# Revit family: IS_Strada_K0776_BIM_BE
name_source: partatom
category: Plumbing Fixtures
revit_build: Autodesk Revit 2015 (Build: 20140606_1530(x64)
units: mm (PartAtom-declared; Revit-internal decimal feet)

## types (1)
- K077601 - Strada Lavabo à poser 50 cm sans vidage
    Accesoires = www.idealstandard.be
    Afwerking = Wit
    Auteur = Ideal Standard Produktions-GmbH
    Barcode = 4015413031363
    Beschrijvinggarantie = Fabrieksgarantie
    BimObjectNaam = ISI_IdealStandard_Lavabo_Strada_K077601
    Breedte = 0
    BrutoGewicht = 0
    Cost = 0 $
    Default Elevation = 0 mm  [stored 0 ft]
    Description = Strada Lavabo à poser 50 cm sans vidage
    Diepte = 0 mm  [stored 0 ft]
    Dimensions = 420 x 500 x 115 mm
    DuurEenheid = jaar
    Eigenschappen = Strada opbouwwastafel 500 mm uit fijne vuurklei. Achterzijde is geglazuurd. Zonder kraangaten of overloop. Te combineren met verhoogde wastafelkraan of muurkraan en een niet afsluitbare waste.
    Garantieonderdelen = 10
    GrootteAfvoergat = 0
    Hauteur = 115 mm
    IfcExportAs = IfcSanitaryTerminalType
    IfcExportType = WASHHANDBASINS
    Installatieinstructies = www.idealstandard.be
    Kleur = Wit
    Largeur = 500 mm
    Lengte = 0 mm  [stored 0 ft]
    Longueur = 420 mm
    Manufacturer = www.idealstandard.be
    Materiaal = fijne vuurklei
    MaterialFinish = IS_IdealStandard_Ceramic_White_Render
    Merk = Ideal Standard
    Model = K077601
    Nettogewicht = 13
    Ophangingwastafel = opbouw
    Productinformatie = www.idealstandard.be
    Telefoonnummer = 0032 2 325 66 00
    Typeconnectie = Sanitair
    Typewastafel = opbouwwastafel
    URL = www.idealstandard.be
    Uniclass2015Beschrijving = Wash basins, sinks and troughs
    Uniclass2015Referentie = Pr_40_20_96
    Uniclass2015Version = Products v1.1
    Urlproducent = www.idealstandard.be
    Versie = 1
    Vervangingskosten = 0
    Verwachtelevensduur = 25 jaar
    Volumeunits = liter
    Vorm = rechthoekig

note: [stored X ft] marks values corroborated as IEEE doubles in the binary element streams (Revit-internal decimal feet)

## geometry (parser evidence)
native form markers: Blend x4, Sweep x2
no freeform markers — native parametric forms only
